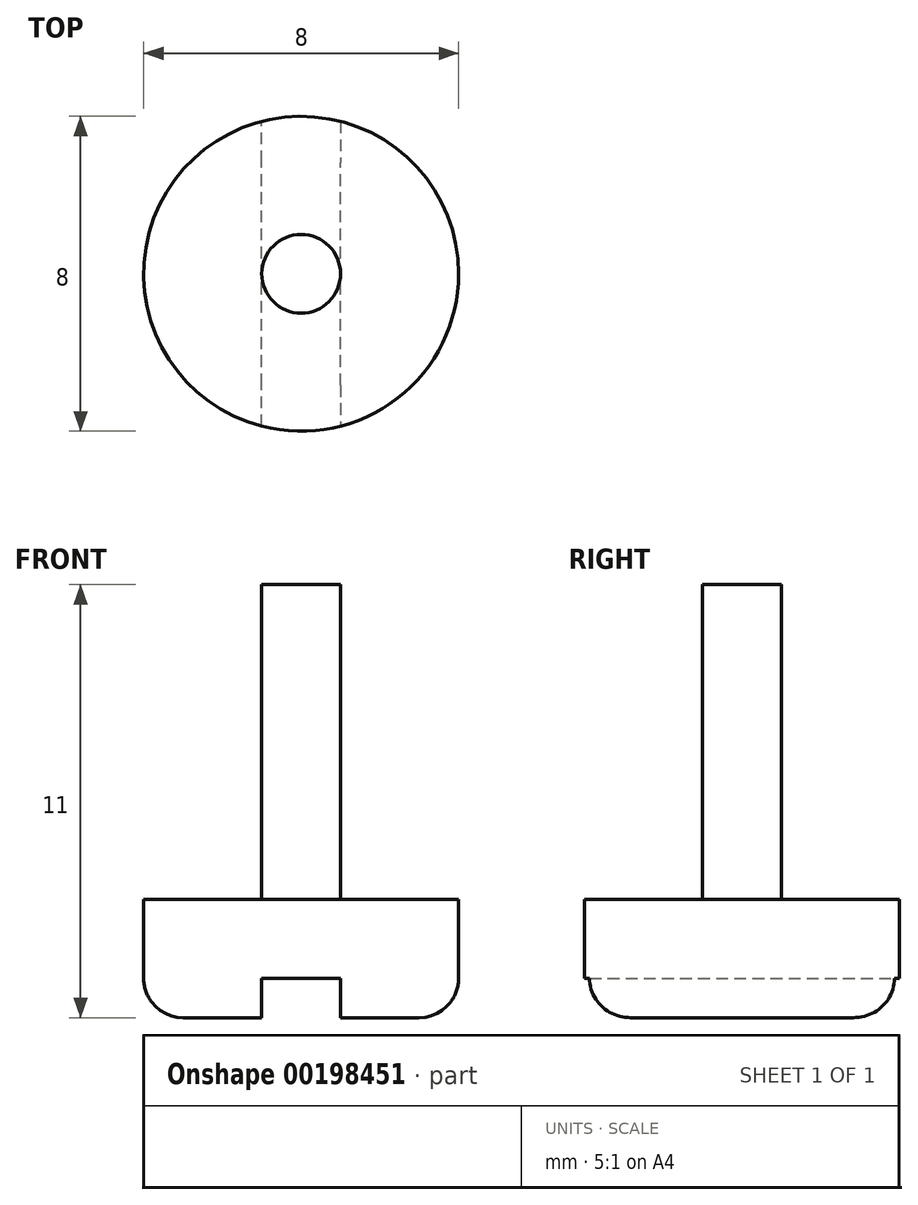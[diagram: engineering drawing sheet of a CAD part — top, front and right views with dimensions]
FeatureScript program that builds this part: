
annotation { "Feature Type Name" : "Feature", "Feature Type Description" : "" }
export const myFeature = defineFeature(function(context is Context, id is Id, definition is map)
    precondition{}
    {
        {
            var Q0;
            Q0=qCreatedBy(makeId("Top.planeOp"),FACE);
            var sketch = newSketch(context, id + "F0", { "sketchPlane" : qUnion([Q0])});
            skCircle(sketch, "E0", {"center": v(0, 0) * mm, "radius": 4 * mm});
            skSolve(sketch);
        }
        {
            var Q0;
            Q0 = qSketchRegion(id + "F0", true);
            extrude(context, id + "F1", {"entities" : qUnion([Q0]), "depth" : 3 * mm});
        }
        {
            var Q0;
            Q0=makeQuery(id+"F1.opExtrude","CAP_FACE",FACE,{"disambiguationData":[OSD([sQuery(id+"F0.wireOp",EDGE,"E0")])],"isStart":false});
            var sketch = newSketch(context, id + "F2", { "sketchPlane" : qUnion([Q0])});
            skCircle(sketch, "E1", {"center": v(0, 0) * mm, "radius": 1 * mm});
            skSolve(sketch);
        }
        {
            var Q0;
            Q0 = qSketchRegion(id + "F2", true);
            extrude(context, id + "F3", {"entities" : qUnion([Q0]), "operationType" : NewBodyOperationType.ADD, "depth" : 8 * mm});
        }
        {
            var Q0;
            Q0=makeQuery(id+"F1.opExtrude","CAP_FACE",FACE,{"disambiguationData":[OSD([sQuery(id+"F0.wireOp",EDGE,"E0")])],"isStart":true});
            var sketch = newSketch(context, id + "F4", { "sketchPlane" : qUnion([Q0])});
            skLineSegment(sketch, "E2.bottom", {"start": v(1, 5.48) * mm, "end": v(-1, 5.48) * mm});
            skLineSegment(sketch, "E2.top", {"start": v(1, -5.48) * mm, "end": v(-1, -5.48) * mm});
            skLineSegment(sketch, "E2.left", {"start": v(1, 5.48) * mm, "end": v(1, -5.48) * mm});
            skLineSegment(sketch, "E2.right", {"start": v(-1, 5.48) * mm, "end": v(-1, -5.48) * mm});
            skPoint(sketch, "E2.middle", {"position": v(0, 0) * mm});
            skSolve(sketch);
        }
        {
            var Q0;
            Q0 = qSketchRegion(id + "F4", true);
            extrude(context, id + "F5", {"entities" : qUnion([Q0]), "operationType" : NewBodyOperationType.REMOVE, "oppositeDirection" : true, "depth" : 1 * mm});
        }
        {
            var Q0;
            {var subQ0=sQuery(id+"F0.wireOp",EDGE,"E0");Q0=makeQuery(id+"F5.boolean.opBoolean","SPLIT",EDGE,{"disambiguationData":[TD([makeQuery(id+"F5.opExtrude","SWEPT_FACE",FACE,{"disambiguationData":[OSD([sQuery(id+"F4.wireOp",EDGE,"E2.right")])]})])],"derivedFrom":makeQuery(id+"F1.opExtrude","CAP_EDGE",EDGE,{"disambiguationData":[OSD([subQ0])],"isStart":true})});}
            var Q1;
            {var subQ0=sQuery(id+"F0.wireOp",EDGE,"E0");Q1=makeQuery(id+"F5.boolean.opBoolean","SPLIT",EDGE,{"disambiguationData":[TD([makeQuery(id+"F5.opExtrude","SWEPT_FACE",FACE,{"disambiguationData":[OSD([sQuery(id+"F4.wireOp",EDGE,"E2.left")])]})])],"derivedFrom":makeQuery(id+"F1.opExtrude","CAP_EDGE",EDGE,{"disambiguationData":[OSD([subQ0])],"isStart":true})});}
            fillet(context, id + "F6", {"entities" : qUnion([Q0, Q1]), "radius" : 1 * mm, "tangentPropagation" : true, "allowEdgeOverflow" : false});
        }
    });
